# Revit family: MBA_Штора_Противопожарная_FireTechnics_БезОрошения
name_source: partatom
category: Двери
revit_build: Autodesk Revit 2016 (Build: 20160314_0715(x64)
units: mm (PartAtom-declared; Revit-internal decimal feet)

## family parameters
Всегда вертикально = Да
Заголовок OmniClass = Rolling Fire Doors
Номер OmniClass = 23.30.10.21.11.11
Общий = Нет
Основа = Стена
При загрузке вырезать с полостями = Нет
Точка расчета площади = Нет

## types (1)
- 4000х4000 EI60
    ADSK_URL страницы изделия = https://mva-rolltor.ru
    ADSK_Единица измерения = шт.
    ADSK_Завод-изготовитель = МВА
    ADSK_Наименование = Противопожарные шторы EI60 (без орошения водой) 4000х4000
    ADSK_Наименование краткое = Противопожарные шторы 4000х4000
    ADSK_Обозначение = ТУ 5284-001-16123348-2020
    ADSK_Предел огнестойкости = EI60
    ADSK_Размер_Высота = 4000 мм
    ADSK_Размер_Ширина = 4000 мм
    URL = https://mva-rolltor.ru
    Аналитическая конструкция = <Нет>
    Высота = 4150 мм
    Высота короба = 150 мм
    Высота направляющих = 80 мм
    Замыкание стены = По основе
    Изготовитель = МВА
    Максимальная высота проема = 5500 мм
    Максимальная ширина проема = 4500 мм
    Материал короба = Сталь_оцинкованная_листовая_1,5мм_МВА
    Материал направляющих = Сталь_оцинкованная_листовая МВА
    Материал полотна = Firetex™ 1100
    Минимальная высота проема = 1000 мм
    Минимальная ширина проема = 1000 мм
    Огнестойкость = EI60
    Описание = Противопожарные шторы (без орошения водой) предназначены разделить помещения на отсеки и не допускать распространение пожара по всему зданию, тем самым, защищая людей и материальные ценности от воздействия огня и дыма.
    Примерная высота = 4000 мм
    Примерная ширина = 4000 мм
    Тип конструкций = Штора противопожарная
    Толщина = 10 мм
    Функция = Внутренние слои
    Ширина = 4120 мм
    Ширина короба = 150 мм
    Ширина направляющих = 60 мм
